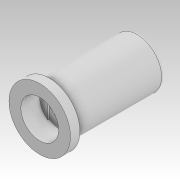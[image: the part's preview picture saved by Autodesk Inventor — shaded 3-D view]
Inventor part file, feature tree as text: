
AUTODESK INVENTOR PART (.ipt)
format: ipt  version: 2022 (Build 260153000, 153)  size: 136,704 bytes
history: native  units: mm
features: sketch x2, revolve x1, fillet x1, extrude x1
ambient origin geometry x8: Origin, YZ Plane, XZ Plane, XY Plane, X Axis, Y Axis, Z Axis, Center Point
bodies: Solid1 (feature_tree)
feature tree (5):
  revolve  "Revolution1"  [1 undecoded]
  fillet  "Fillet1"  Radius=1.0mm
  extrude  "Extrusion1"  Depth=14.5mm
  sketch  "Sketch1"  dims[d0=1.7mm d1=3.9mm d2=1.0mm]
  sketch  "Sketch2"  dims[d3=1.5mm d4=14.5mm d5=90.0deg d6=3.0mm d7=3.0mm d8=0.5mm d9=0.2mm d10=0.0mm]
note: 1 required parameter value undecoded (feature->parameter linkage not recoverable at this tier; creation-order binding heuristic only, values carry confidence <= 0.55)
